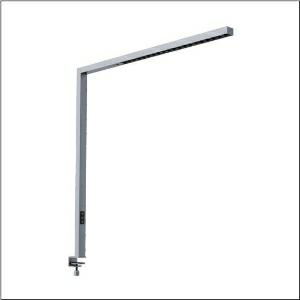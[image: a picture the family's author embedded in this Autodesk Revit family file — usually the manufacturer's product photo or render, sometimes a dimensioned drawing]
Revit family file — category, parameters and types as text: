
# Revit family: silica_r__31_desk_51my52ga3cs_3f63
name_source: partatom
category: Lighting Fixtures
units: mm (PartAtom-declared; Revit-internal decimal feet)

## family parameters
Cut with Voids When Loaded = No
Host = Face
Light Source = No
Part Type = Normal
Room Calculation Point = No
Round Connector Dimension = Use Diameter
Shared = No

## types (1)
- Silica® 31 Desk (1 x LED, 10300 lm, 75 W, 3000K)
    Apparent Load = 75 VA
    CIE Flux Codes = 86 100 100 24 100
    Color Rendering = 80
    Color Temperature = 3000K
    Default Elevation = 1800 mm
    Description = Silica® 31 Desk, desktop luminaire, secondary optical cover: cover panel, of PMMA, light emission: direct/indirect distribution, primary light characteristic: symmetric, installation type: as desk luminaire, LED, rated luminous flux: 10.300lm, luminous efficacy: 137lm/W, light colour: 830, colour temperature: 3000K, control gear: Touchdim, daylight-dependent control, with cable with plug, mains connection: 230V, AC, 50Hz, connection cable pre-assembled, rated input power: 75W, luminaire head, of aluminium, metallic grey (RAL 9006), length: 1.203mm, width: 52mm, supporting column, angular, of aluminium, metallic grey (RAL 9006), baseplate, of steel, metallic grey (RAL 9006), protection rating (complete): IP20, insulation class (complete): insulation class I (protective earthing), certification: CE, permissible operating ambient temperature: -20..+40°C, standard: EN 50419, packaging unit: 1 piece
    Height = 36 mm
    Lamp = 1 x LED
    Lamp Light Flux = 10300 lm
    Lamp Power = 75 W
    Lamp count = 1
    Length = 1203 mm
    Luminous efficacy = 137 lm/W
    Manufacturer = Siteco
    ModVariant = No
    Model = 51MY52GA3CS
    Mounting Place = Floor
    Mounting Type = Freestanding
    Number of Poles = 1
    OnlyDefault = Yes
    Power Factor = 1
    Product Name = Silica® 31 Desk
    Product group = desktop luminaire
    ProductGroupID = 1303
    Protection Class = Protection class I
    Protection Degree = IP 20
    RLX_Detail_Level = 1
    RLX_Emergency_Light_Flux = 0 lm
    RLX_Emergency_Type = 0
    RLX_Emergency_Type_DB = No
    RlxData = <blob elided: 19649 chars, md5=dd22f1c8>
    Socket = socket
    Standby Power = 0 W
    System Light Flux = 10300 lm
    System Power = 75 W
    Type Comments = Product without accessories
    Type Image = l_1275333.jpg
    URL = http://relux.com
    VarID = ---
    Voltage = 0 V
    Weight = 0.00 kg
    Width = 52 mm  [stored 0.170604 ft]

note: [stored X ft] marks values corroborated as IEEE doubles in the binary element streams (Revit-internal decimal feet)

## geometry (parser evidence)
native form markers: Blend x4, Sweep x15
no freeform markers — native parametric forms only
